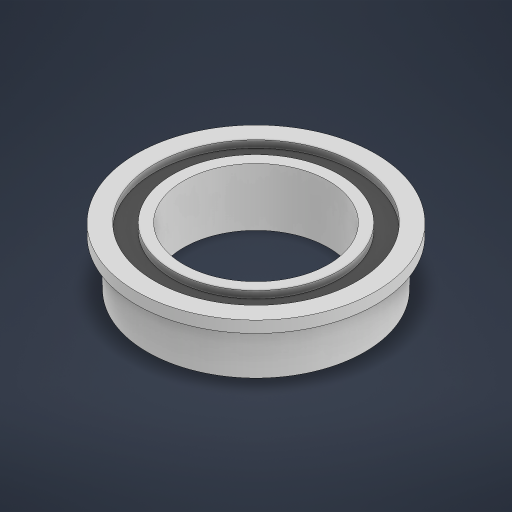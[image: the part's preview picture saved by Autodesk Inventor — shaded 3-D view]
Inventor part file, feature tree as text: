
AUTODESK INVENTOR PART (.ipt)
format: ipt  version: 2024 (Build 280153000, 153)  size: 247,296 bytes
history: native  units: in
note: dims shown in document units (in); Inventor stores cm internally (conversion verified against a paired STEP export)
features: extrude x4, sketch x4, projected_geometry x1
ambient origin geometry x8: Origin, YZ Plane, XZ Plane, XY Plane, X Axis, Y Axis, Z Axis, Center Point
bodies: Solid1 (feature_tree)
feature tree (9):
  extrude  "Extrusion1"  Depth=0.3937in
  extrude  "Extrusion2"  Depth=0.126in
  extrude  "Extrusion3"  Depth=0.0315in
  extrude  "Extrusion4"  Depth=0.0197in TaperAngle=0.0deg
  sketch  "Sketch1"  dims[d0=0.3937in d1=0.5906in]
  sketch  "Sketch2"  dims[d2=0.126in d3=0.0in d4=0.6496in]
  sketch  "Sketch3"  dims[d5=0.0315in d6=0.0in d7=0.4528in]
  sketch  "Sketch4"  dims[d8=0.5512in d9=0.0197in d10=0.0in d11=0.0197in d12=0.0in]
  projected_geometry  "Projected Loop1"
